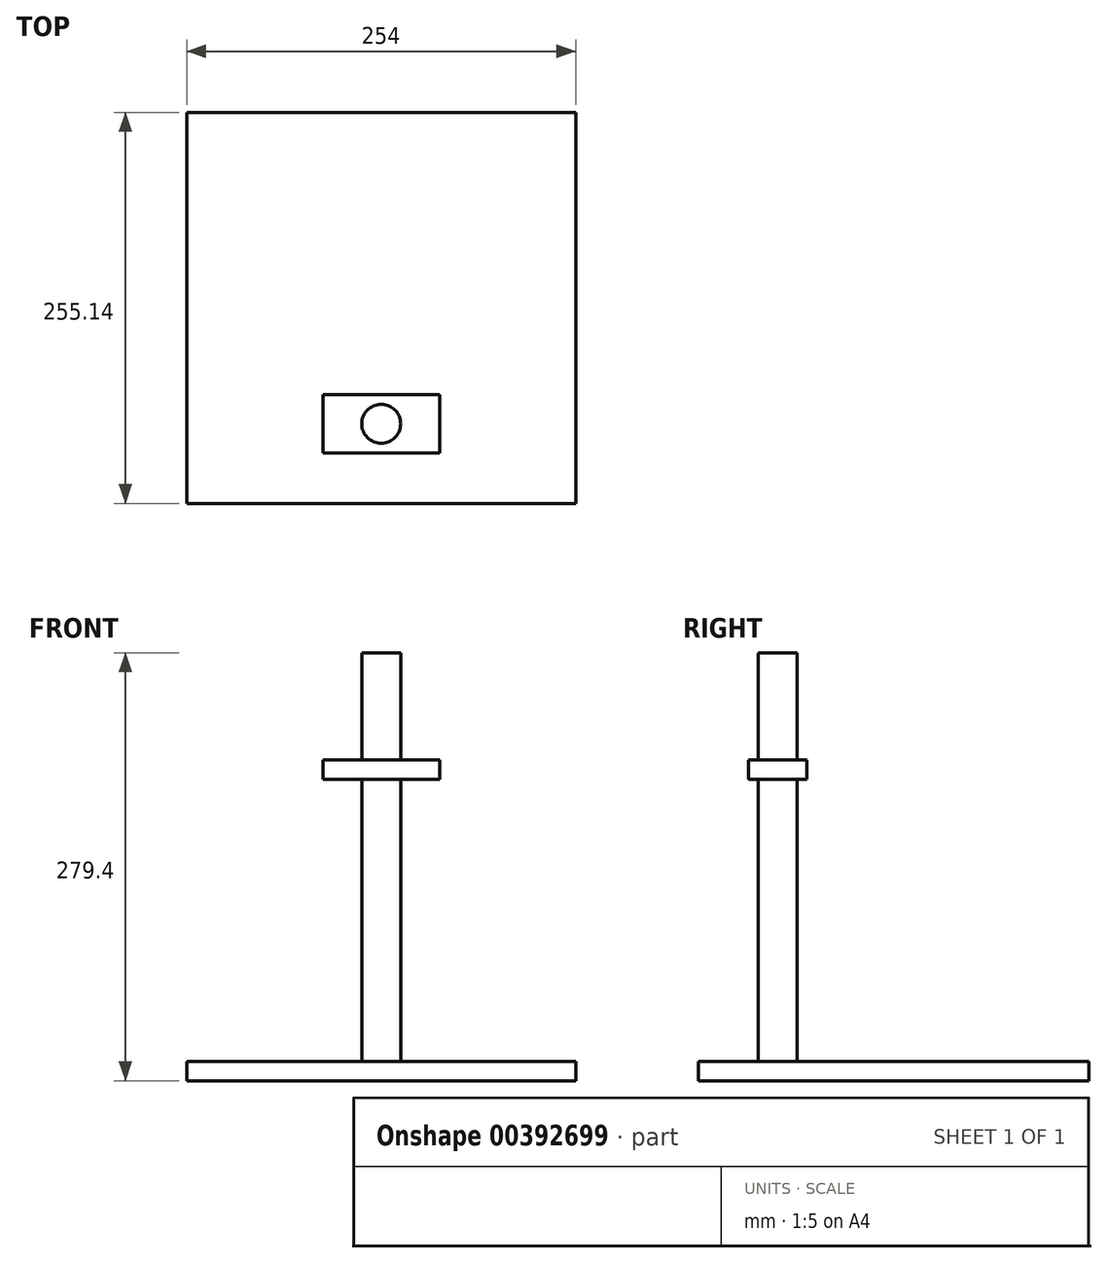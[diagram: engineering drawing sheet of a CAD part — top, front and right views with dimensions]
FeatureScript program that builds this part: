
annotation { "Feature Type Name" : "Feature", "Feature Type Description" : "" }
export const myFeature = defineFeature(function(context is Context, id is Id, definition is map)
    precondition{}
    {
        {
            var Q0;
            Q0=qCreatedBy(makeId("Top.planeOp"),FACE);
            var sketch = newSketch(context, id + "F0", { "sketchPlane" : qUnion([Q0])});
            skCircle(sketch, "E0", {"center": v(0, 0) * mm, "radius": 12.7 * mm});
            skSolve(sketch);
        }
        {
            var Q0;
            Q0 = qSketchRegion(id + "F0", true);
            extrude(context, id + "F1", {"entities" : qUnion([Q0]), "depth" : 266.7 * mm});
        }
        {
            var Q0;
            Q0=qCreatedBy(makeId("Top.planeOp"),FACE);
            cPlane(context, id + "F2", {"entities" : qUnion([Q0]), "cplaneType" : CPlaneType.OFFSET, "offset" : 196.85 * mm, "width" : 152.4 * mm, "height" : 152.4 * mm});
        }
        {
            var Q0;
            Q0=qCreatedBy(id+"F2.planeOp",FACE);
            var sketch = newSketch(context, id + "F3", { "sketchPlane" : qUnion([Q0])});
            skLineSegment(sketch, "E1.bottom", {"start": v(38.1, -19.05) * mm, "end": v(-38.1, -19.05) * mm});
            skLineSegment(sketch, "E1.top", {"start": v(38.1, 19.05) * mm, "end": v(-38.1, 19.05) * mm});
            skLineSegment(sketch, "E1.left", {"start": v(38.1, -19.05) * mm, "end": v(38.1, 19.05) * mm});
            skLineSegment(sketch, "E1.right", {"start": v(-38.1, -19.05) * mm, "end": v(-38.1, 19.05) * mm});
            skPoint(sketch, "E1.middle", {"position": v(0, 0) * mm});
            skSolve(sketch);
        }
        {
            var Q0;
            Q0=makeQuery(id+"F3.imprint","IMPRINT",FACE,{"disambiguationData":[TD([[makeQuery(id+"F3.imprint","IMPRINT",EDGE,{"derivedFrom":sQuery(id+"F3.wireOp",EDGE,"E1.bottom")}),-1.0]])]});
            extrude(context, id + "F4", {"entities" : qUnion([Q0]), "operationType" : NewBodyOperationType.ADD, "oppositeDirection" : true, "depth" : 12.7 * mm});
        }
        {
            var Q0;
            Q0=makeQuery(id+"F1.opExtrude","CAP_FACE",FACE,{"disambiguationData":[OSD([sQuery(id+"F0.wireOp",EDGE,"E0")])],"isStart":true});
            var sketch = newSketch(context, id + "F5", { "sketchPlane" : qUnion([Q0])});
            skPoint(sketch, "E2.middle", {"position": v(0, 0) * mm});
            skLineSegment(sketch, "E3.bottom", {"start": v(-127, 51.94) * mm, "end": v(127, 51.94) * mm});
            skLineSegment(sketch, "E3.top", {"start": v(-127, -203.2) * mm, "end": v(127, -203.2) * mm});
            skLineSegment(sketch, "E3.left", {"start": v(-127, 51.94) * mm, "end": v(-127, -203.2) * mm});
            skLineSegment(sketch, "E3.right", {"start": v(127, 51.94) * mm, "end": v(127, -203.2) * mm});
            skSolve(sketch);
        }
        {
            var Q0;
            Q0 = qSketchRegion(id + "F5", true);
            extrude(context, id + "F6", {"entities" : qUnion([Q0]), "operationType" : NewBodyOperationType.ADD, "depth" : 12.7 * mm});
        }
    });
